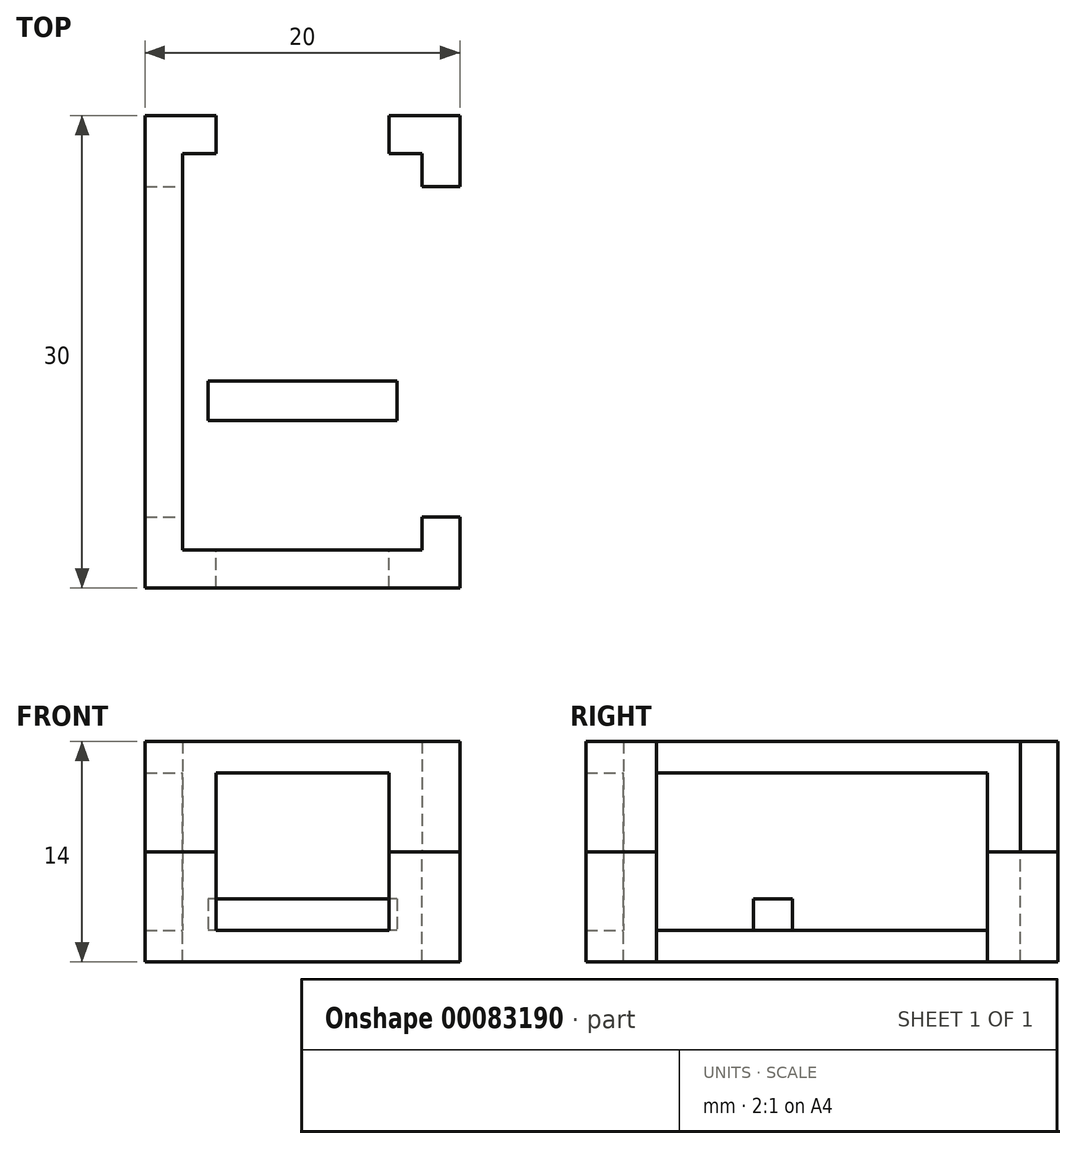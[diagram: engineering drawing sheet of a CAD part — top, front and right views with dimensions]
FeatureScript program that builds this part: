
annotation { "Feature Type Name" : "Feature", "Feature Type Description" : "" }
export const myFeature = defineFeature(function(context is Context, id is Id, definition is map)
    precondition{}
    {
        {
            var Q0;
            Q0=qCreatedBy(makeId("Top.planeOp"),FACE);
            var sketch = newSketch(context, id + "F0", { "sketchPlane" : qUnion([Q0])});
            skLineSegment(sketch, "E0.bottom", {"start": v(-38.64, -31.51) * mm, "end": v(-53.84, -31.51) * mm});
            skLineSegment(sketch, "E0.top", {"start": v(-38.64, -6.31) * mm, "end": v(-53.84, -6.31) * mm});
            skLineSegment(sketch, "E0.left", {"start": v(-38.64, -31.51) * mm, "end": v(-38.64, -6.31) * mm});
            skLineSegment(sketch, "E0.right", {"start": v(-53.84, -31.51) * mm, "end": v(-53.84, -6.31) * mm});
            skPoint(sketch, "E1", {"position": v(-49.44, -6.31) * mm});
            skPoint(sketch, "E2", {"position": v(-38.64, -27.41) * mm});
            skLineSegment(sketch, "E3.1.0.0", {"start": v(-38.64, -26.16) * mm, "end": v(-38.64, -25.16) * mm});
            skPoint(sketch, "E3.1.0.1", {"position": v(-38.64, -26.16) * mm});
            skLineSegment(sketch, "E3.2.0.0", {"start": v(-38.64, -24.91) * mm, "end": v(-38.64, -23.91) * mm});
            skPoint(sketch, "E3.2.0.1", {"position": v(-38.64, -24.91) * mm});
            skLineSegment(sketch, "E3.3.0.0", {"start": v(-38.64, -23.66) * mm, "end": v(-38.64, -22.66) * mm});
            skPoint(sketch, "E3.3.0.1", {"position": v(-38.64, -23.66) * mm});
            skLineSegment(sketch, "E4.0.8.0", {"start": v(-38.64, -17.41) * mm, "end": v(-38.64, -16.41) * mm});
            skPoint(sketch, "E4.3.8.0", {"position": v(-38.64, -17.41) * mm});
            skLineSegment(sketch, "E4.0.9.0", {"start": v(-38.64, -16.16) * mm, "end": v(-38.64, -15.16) * mm});
            skPoint(sketch, "E4.3.9.0", {"position": v(-38.64, -16.16) * mm});
            skLineSegment(sketch, "E5.bottom", {"start": v(-49.44, -6.31) * mm, "end": v(-48.44, -6.31) * mm});
            skPoint(sketch, "E6.1.0.1", {"position": v(-48.19, -6.31) * mm});
            skLineSegment(sketch, "E6.1.0.4", {"start": v(-48.19, -6.31) * mm, "end": v(-47.19, -6.31) * mm});
            skPoint(sketch, "E6.2.0.1", {"position": v(-46.94, -6.31) * mm});
            skLineSegment(sketch, "E6.2.0.4", {"start": v(-46.94, -6.31) * mm, "end": v(-45.94, -6.31) * mm});
            skPoint(sketch, "E6.3.0.1", {"position": v(-45.69, -6.31) * mm});
            skLineSegment(sketch, "E6.3.0.4", {"start": v(-45.69, -6.31) * mm, "end": v(-44.69, -6.31) * mm});
            skPoint(sketch, "E6.4.0.1", {"position": v(-44.44, -6.31) * mm});
            skLineSegment(sketch, "E6.4.0.4", {"start": v(-44.44, -6.31) * mm, "end": v(-43.44, -6.31) * mm});
            skLineSegment(sketch, "E7.bottom", {"start": v(-36.24, -33.91) * mm, "end": v(-56.24, -33.91) * mm});
            skLineSegment(sketch, "E7.top", {"start": v(-36.24, -3.91) * mm, "end": v(-56.24, -3.91) * mm});
            skLineSegment(sketch, "E7.left", {"start": v(-36.24, -33.91) * mm, "end": v(-36.24, -3.91) * mm});
            skLineSegment(sketch, "E7.right", {"start": v(-56.24, -33.91) * mm, "end": v(-56.24, -3.91) * mm});
            skLineSegment(sketch, "E8.bottom", {"start": v(-42.24, -16.16) * mm, "end": v(-50.24, -16.16) * mm});
            skLineSegment(sketch, "E8.top", {"start": v(-42.24, -8.66) * mm, "end": v(-50.24, -8.66) * mm});
            skLineSegment(sketch, "E8.left", {"start": v(-42.24, -16.16) * mm, "end": v(-42.24, -8.66) * mm});
            skLineSegment(sketch, "E8.right", {"start": v(-50.24, -16.16) * mm, "end": v(-50.24, -8.66) * mm});
            skPoint(sketch, "E9", {"position": v(-39.24, -24.41) * mm});
            skPoint(sketch, "E9.positionSnap0", {"position": v(-39.84, -24.41) * mm});
            skPoint(sketch, "E9.positionSnap1", {"position": v(-39.24, -24.91) * mm});
            skPoint(sketch, "E10", {"position": v(-39.24, -23.16) * mm});
            skPoint(sketch, "E10.positionSnap0", {"position": v(-39.84, -23.16) * mm});
            skPoint(sketch, "E10.positionSnap1", {"position": v(-39.24, -23.66) * mm});
            skPoint(sketch, "E11", {"position": v(-39.24, -16.91) * mm});
            skPoint(sketch, "E11.positionSnap0", {"position": v(-39.84, -16.91) * mm});
            skPoint(sketch, "E11.positionSnap1", {"position": v(-39.24, -17.41) * mm});
            skPoint(sketch, "E12", {"position": v(-39.24, -15.66) * mm});
            skPoint(sketch, "E12.positionSnap0", {"position": v(-39.84, -15.66) * mm});
            skPoint(sketch, "E12.positionSnap1", {"position": v(-39.24, -16.16) * mm});
            skPoint(sketch, "E13", {"position": v(-43.94, -6.91) * mm});
            skPoint(sketch, "E13.positionSnap0", {"position": v(-43.94, -7.51) * mm});
            skPoint(sketch, "E13.positionSnap1", {"position": v(-43.44, -6.91) * mm});
            skPoint(sketch, "E14", {"position": v(-45.19, -6.91) * mm});
            skPoint(sketch, "E14.positionSnap0", {"position": v(-45.19, -7.51) * mm});
            skPoint(sketch, "E14.positionSnap1", {"position": v(-45.69, -6.91) * mm});
            skPoint(sketch, "E15", {"position": v(-46.44, -6.91) * mm});
            skPoint(sketch, "E15.positionSnap0", {"position": v(-46.44, -7.51) * mm});
            skPoint(sketch, "E15.positionSnap1", {"position": v(-46.94, -6.91) * mm});
            skPoint(sketch, "E16", {"position": v(-47.69, -6.91) * mm});
            skPoint(sketch, "E16.positionSnap0", {"position": v(-47.69, -7.51) * mm});
            skPoint(sketch, "E16.positionSnap1", {"position": v(-47.19, -6.91) * mm});
            skPoint(sketch, "E17", {"position": v(-48.94, -6.91) * mm});
            skPoint(sketch, "E17.positionSnap0", {"position": v(-48.94, -6.31) * mm});
            skPoint(sketch, "E17.positionSnap1", {"position": v(-48.44, -6.91) * mm});
            skLineSegment(sketch, "E18", {"start": v(-56.24, -29.41) * mm, "end": v(-53.84, -29.41) * mm});
            skLineSegment(sketch, "E19", {"start": v(-51.74, -33.91) * mm, "end": v(-51.74, -31.51) * mm});
            skLineSegment(sketch, "E20.trimOffspring", {"start": v(-38.64, -29.41) * mm, "end": v(-36.24, -29.41) * mm});
            skLineSegment(sketch, "E21.trimOffspring", {"start": v(-51.74, -6.31) * mm, "end": v(-51.74, -3.91) * mm});
            skLineSegment(sketch, "E22.MirrorCS", {"start": v(-56.24, -8.41) * mm, "end": v(-53.84, -8.41) * mm});
            skLineSegment(sketch, "E23.MirrorCS", {"start": v(-38.64, -8.41) * mm, "end": v(-36.24, -8.41) * mm});
            skLineSegment(sketch, "E24.MirrorCS", {"start": v(-40.74, -33.91) * mm, "end": v(-40.74, -31.51) * mm});
            skLineSegment(sketch, "E25.MirrorCS", {"start": v(-40.74, -6.31) * mm, "end": v(-40.74, -3.91) * mm});
            skLineSegment(sketch, "E26", {"start": v(-53.84, -19.28) * mm, "end": v(-38.64, -19.28) * mm, "construction": true});
            skLineSegment(sketch, "E27", {"start": v(-53.84, -22.02) * mm, "end": v(-38.64, -22.02) * mm, "construction": true});
            skLineSegment(sketch, "E28", {"start": v(-53.84, -25.38) * mm, "end": v(-38.64, -25.38) * mm, "construction": true});
            skLineSegment(sketch, "E29", {"start": v(-53.84, -28.17) * mm, "end": v(-38.64, -28.17) * mm, "construction": true});
            skPoint(sketch, "E30", {"position": v(-49.84, -19.28) * mm});
            skPoint(sketch, "E31", {"position": v(-48.59, -19.28) * mm});
            skPoint(sketch, "E32", {"position": v(-43.89, -19.28) * mm});
            skPoint(sketch, "E33", {"position": v(-49.84, -22.02) * mm});
            skPoint(sketch, "E34", {"position": v(-48.59, -22.02) * mm});
            skPoint(sketch, "E35", {"position": v(-42.64, -22.02) * mm});
            skPoint(sketch, "E36", {"position": v(-43.89, -22.02) * mm});
            skPoint(sketch, "E37", {"position": v(-49.84, -25.38) * mm});
            skPoint(sketch, "E38", {"position": v(-48.59, -25.38) * mm});
            skPoint(sketch, "E39", {"position": v(-43.89, -25.38) * mm});
            skPoint(sketch, "E40", {"position": v(-42.64, -25.38) * mm});
            skPoint(sketch, "E41", {"position": v(-42.64, -19.28) * mm});
            skPoint(sketch, "E42", {"position": v(-39.24, -26.91) * mm});
            skPoint(sketch, "E43", {"position": v(-39.24, -25.66) * mm});
            skSolve(sketch);
        }
        {
            var Q0;
            Q0=makeQuery(id+"F0.imprint","IMPRINT",FACE,{"disambiguationData":[TD([[makeQuery(id+"F0.imprint","IMPRINT",EDGE,{"derivedFrom":sQuery(id+"F0.wireOp",EDGE,"5d814dad-614f-4d97-b61d-e02d43bfdc46")}),-1.0]])]});
            var Q1;
            {var subQ0=sQuery(id+"F0.wireOp",EDGE,"E18");Q1=makeQuery(id+"F0.imprint","IMPRINT",FACE,{"disambiguationData":[TD([[makeQuery(id+"F0.imprint","IMPRINT",EDGE,{"derivedFrom":subQ0}),1.0]])]});}
            var Q2;
            {var subQ0=sQuery(id+"F0.wireOp",EDGE,"E19");Q2=makeQuery(id+"F0.imprint","IMPRINT",FACE,{"disambiguationData":[TD([[makeQuery(id+"F0.imprint","IMPRINT",EDGE,{"derivedFrom":subQ0}),-1.0]])]});}
            var Q3;
            {var subQ3=sQuery(id+"F0.wireOp",EDGE,"E18");Q3=makeQuery(id+"F0.imprint","IMPRINT",FACE,{"disambiguationData":[TD([[makeQuery(id+"F0.imprint","IMPRINT",EDGE,{"derivedFrom":subQ3}),-1.0]])]});}
            var Q4;
            {var subQ4=sQuery(id+"F0.wireOp",EDGE,"E20.trimOffspring");Q4=makeQuery(id+"F0.imprint","IMPRINT",FACE,{"disambiguationData":[TD([[makeQuery(id+"F0.imprint","IMPRINT",EDGE,{"derivedFrom":subQ4}),-1.0]])]});}
            var Q5;
            {var subQ4=sQuery(id+"F0.wireOp",EDGE,"E3.1.0.0");Q5=makeQuery(id+"F0.imprint","IMPRINT",FACE,{"disambiguationData":[TD([[makeQuery(id+"F0.imprint","IMPRINT",EDGE,{"derivedFrom":subQ4}),-1.0]])]});}
            var Q6;
            {var subQ3=sQuery(id+"F0.wireOp",EDGE,"E23.MirrorCS");Q6=makeQuery(id+"F0.imprint","IMPRINT",FACE,{"disambiguationData":[TD([[makeQuery(id+"F0.imprint","IMPRINT",EDGE,{"derivedFrom":subQ3}),1.0]])]});}
            var Q7;
            {var subQ0=sQuery(id+"F0.wireOp",EDGE,"E5.bottom");Q7=makeQuery(id+"F0.imprint","IMPRINT",FACE,{"disambiguationData":[TD([[makeQuery(id+"F0.imprint","IMPRINT",EDGE,{"derivedFrom":subQ0}),1.0]])]});}
            var Q8;
            {var subQ7=sQuery(id+"F0.wireOp",EDGE,"E21.trimOffspring");Q8=makeQuery(id+"F0.imprint","IMPRINT",FACE,{"disambiguationData":[TD([[makeQuery(id+"F0.imprint","IMPRINT",EDGE,{"derivedFrom":subQ7}),1.0]])]});}
            var Q9;
            {var subQ4=sQuery(id+"F0.wireOp",EDGE,"E3.1.0.0");Q9=makeQuery(id+"F0.imprint","IMPRINT",FACE,{"disambiguationData":[TD([[makeQuery(id+"F0.imprint","IMPRINT",EDGE,{"derivedFrom":subQ4}),1.0]])]});}
            extrude(context, id + "F1", {"entities" : qUnion([Q0, Q1, Q2, Q3, Q4, Q5, Q6, Q7, Q8, Q9]), "oppositeDirection" : true, "depth" : 2 * mm});
        }
        {
            var Q0;
            {var subQ4=sQuery(id+"F0.wireOp",EDGE,"E21.trimOffspring");Q0=makeQuery(id+"F0.imprint","IMPRINT",FACE,{"disambiguationData":[TD([[makeQuery(id+"F0.imprint","IMPRINT",EDGE,{"derivedFrom":subQ4}),1.0]])]});}
            var Q1;
            {var subQ3=sQuery(id+"F0.wireOp",EDGE,"E23.MirrorCS");Q1=makeQuery(id+"F0.imprint","IMPRINT",FACE,{"disambiguationData":[TD([[makeQuery(id+"F0.imprint","IMPRINT",EDGE,{"derivedFrom":subQ3}),1.0]])]});}
            var Q2;
            {var subQ3=sQuery(id+"F0.wireOp",EDGE,"E20.trimOffspring");Q2=makeQuery(id+"F0.imprint","IMPRINT",FACE,{"disambiguationData":[TD([[makeQuery(id+"F0.imprint","IMPRINT",EDGE,{"derivedFrom":subQ3}),-1.0]])]});}
            var Q3;
            {var subQ3=sQuery(id+"F0.wireOp",EDGE,"E18");Q3=makeQuery(id+"F0.imprint","IMPRINT",FACE,{"disambiguationData":[TD([[makeQuery(id+"F0.imprint","IMPRINT",EDGE,{"derivedFrom":subQ3}),-1.0]])]});}
            extrude(context, id + "F2", {"entities" : qUnion([Q0, Q1, Q2, Q3]), "operationType" : NewBodyOperationType.ADD, "depth" : 5 * mm});
        }
        {
            var Q0;
            Q0=sQuery(id+"F0.wireOp",VERTEX,"E9");
            var Q1;
            Q1=sQuery(id+"F0.wireOp",VERTEX,"E10");
            var Q2;
            Q2=sQuery(id+"F0.wireOp",VERTEX,"E11");
            var Q3;
            Q3=sQuery(id+"F0.wireOp",VERTEX,"E12");
            var Q4;
            Q4=sQuery(id+"F0.wireOp",VERTEX,"E13");
            var Q5;
            Q5=sQuery(id+"F0.wireOp",VERTEX,"E14");
            var Q6;
            Q6=sQuery(id+"F0.wireOp",VERTEX,"E15");
            var Q7;
            Q7=sQuery(id+"F0.wireOp",VERTEX,"E16");
            var Q8;
            Q8=sQuery(id+"F0.wireOp",VERTEX,"E17");
            var Q9;
            Q9=sQuery(id+"F0.wireOp",VERTEX,"E43");
            var Q10;
            Q10=sQuery(id+"F0.wireOp",VERTEX,"E42");
            var Q11;
            Q11=makeQuery(id+"F1.opExtrude","SWEPT_BODY",BODY,{"disambiguationData":[OSD([sQuery(id+"F0.wireOp",EDGE,"E7.bottom"),sQuery(id+"F0.wireOp",EDGE,"E7.top"),sQuery(id+"F0.wireOp",EDGE,"E7.left"),sQuery(id+"F0.wireOp",EDGE,"E7.right"),sQuery(id+"F0.wireOp",EDGE,"E8.bottom"),sQuery(id+"F0.wireOp",EDGE,"E8.top"),sQuery(id+"F0.wireOp",EDGE,"E8.left"),sQuery(id+"F0.wireOp",EDGE,"E8.right")])]});
            hole(context, id + "F3", {"style" : HoleStyle.SIMPLE, "endStyle" : HoleEndStyle.THROUGH, "holeDiameter" : 1.1 * mm, "locations" : qUnion([Q0, Q1, Q2, Q3, Q4, Q5, Q6, Q7, Q8, Q9, Q10]), "scope" : qUnion([Q11]), "isTappedThrough" : true});
        }
        {
            var Q0;
            Q0=sQuery(id+"F0.wireOp",VERTEX,"E30");
            var Q1;
            Q1=sQuery(id+"F0.wireOp",VERTEX,"E31");
            var Q2;
            Q2=sQuery(id+"F0.wireOp",VERTEX,"E32");
            var Q3;
            Q3=sQuery(id+"F0.wireOp",VERTEX,"E41");
            var Q4;
            Q4=sQuery(id+"F0.wireOp",VERTEX,"E33");
            var Q5;
            Q5=sQuery(id+"F0.wireOp",VERTEX,"E34");
            var Q6;
            Q6=sQuery(id+"F0.wireOp",VERTEX,"E36");
            var Q7;
            Q7=sQuery(id+"F0.wireOp",VERTEX,"E35");
            var Q8;
            Q8=makeQuery(id+"F1.opExtrude","SWEPT_BODY",BODY,{"disambiguationData":[OSD([sQuery(id+"F0.wireOp",EDGE,"E7.bottom"),sQuery(id+"F0.wireOp",EDGE,"E7.top"),sQuery(id+"F0.wireOp",EDGE,"E7.left"),sQuery(id+"F0.wireOp",EDGE,"E7.right"),sQuery(id+"F0.wireOp",EDGE,"E8.bottom"),sQuery(id+"F0.wireOp",EDGE,"E8.top"),sQuery(id+"F0.wireOp",EDGE,"E8.left"),sQuery(id+"F0.wireOp",EDGE,"E8.right")])]});
            hole(context, id + "F4", {"style" : HoleStyle.SIMPLE, "endStyle" : HoleEndStyle.THROUGH, "holeDiameter" : 1.1 * mm, "locations" : qUnion([Q0, Q1, Q2, Q3, Q4, Q5, Q6, Q7]), "scope" : qUnion([Q8]), "isTappedThrough" : true});
        }
        {
            var Q0;
            Q0=sQuery(id+"F0.wireOp",VERTEX,"E37");
            var Q1;
            Q1=sQuery(id+"F0.wireOp",VERTEX,"E38");
            var Q2;
            Q2=sQuery(id+"F0.wireOp",VERTEX,"E39");
            var Q3;
            Q3=sQuery(id+"F0.wireOp",VERTEX,"E40");
            var Q4;
            Q4=makeQuery(id+"F1.opExtrude","SWEPT_BODY",BODY,{"disambiguationData":[OSD([sQuery(id+"F0.wireOp",EDGE,"E7.bottom"),sQuery(id+"F0.wireOp",EDGE,"E7.top"),sQuery(id+"F0.wireOp",EDGE,"E7.left"),sQuery(id+"F0.wireOp",EDGE,"E7.right"),sQuery(id+"F0.wireOp",EDGE,"E8.bottom"),sQuery(id+"F0.wireOp",EDGE,"E8.top"),sQuery(id+"F0.wireOp",EDGE,"E8.left"),sQuery(id+"F0.wireOp",EDGE,"E8.right")])]});
            hole(context, id + "F5", {"style" : HoleStyle.SIMPLE, "endStyle" : HoleEndStyle.THROUGH, "holeDiameter" : 1 * mm, "locations" : qUnion([Q0, Q1, Q2, Q3]), "scope" : qUnion([Q4]), "isTappedThrough" : true});
        }
        {
            var Q0;
            Q0=makeQuery(id+"F1.opExtrude","CAP_FACE",FACE,{"disambiguationData":[OSD([sQuery(id+"F0.wireOp",EDGE,"E7.bottom"),sQuery(id+"F0.wireOp",EDGE,"E7.top"),sQuery(id+"F0.wireOp",EDGE,"E7.left"),sQuery(id+"F0.wireOp",EDGE,"E7.right"),sQuery(id+"F0.wireOp",EDGE,"E8.bottom"),sQuery(id+"F0.wireOp",EDGE,"E8.top"),sQuery(id+"F0.wireOp",EDGE,"E8.left"),sQuery(id+"F0.wireOp",EDGE,"E8.right")])],"isStart":true});
            var sketch = newSketch(context, id + "F6", { "sketchPlane" : qUnion([Q0])});
            skLineSegment(sketch, "E44.bottom", {"start": v(-41.24, -22.67) * mm, "end": v(-51.24, -22.67) * mm});
            skLineSegment(sketch, "E44.top", {"start": v(-41.24, -21.37) * mm, "end": v(-51.24, -21.37) * mm});
            skLineSegment(sketch, "E44.left", {"start": v(-41.24, -22.67) * mm, "end": v(-41.24, -21.37) * mm});
            skLineSegment(sketch, "E44.right", {"start": v(-51.24, -22.67) * mm, "end": v(-51.24, -21.37) * mm});
            skPoint(sketch, "E44.middle", {"position": v(-46.24, -22.02) * mm});
            skPoint(sketch, "E44.middle.positionSnap0", {"position": v(-46.24, -16.16) * mm});
            skPoint(sketch, "E44.centerSnap0", {"position": v(-46.24, -16.16) * mm});
            skPoint(sketch, "E45", {"position": v(-43.89, -22.02) * mm});
            skLineSegment(sketch, "E46.bottom", {"start": v(-40.24, -23.27) * mm, "end": v(-52.24, -23.27) * mm});
            skLineSegment(sketch, "E46.top", {"start": v(-40.24, -20.77) * mm, "end": v(-52.24, -20.77) * mm});
            skLineSegment(sketch, "E46.left", {"start": v(-40.24, -23.27) * mm, "end": v(-40.24, -20.77) * mm});
            skLineSegment(sketch, "E46.right", {"start": v(-52.24, -23.27) * mm, "end": v(-52.24, -20.77) * mm});
            skLineSegment(sketch, "E47", {"start": v(-41.24, -21.42) * mm, "end": v(-46.24, -21.42) * mm});
            skLineSegment(sketch, "E48", {"start": v(-46.24, -21.37) * mm, "end": v(-46.24, -21.42) * mm});
            skLineSegment(sketch, "E49", {"start": v(-46.24, -22.62) * mm, "end": v(-41.24, -22.62) * mm});
            skLineSegment(sketch, "E50.trimOffspring", {"start": v(-46.24, -22.62) * mm, "end": v(-46.24, -22.67) * mm});
            skSolve(sketch);
        }
        {
            var Q0;
            Q0=makeQuery(id+"F1.opExtrude","CAP_FACE",FACE,{"disambiguationData":[OSD([sQuery(id+"F0.wireOp",EDGE,"E7.bottom"),sQuery(id+"F0.wireOp",EDGE,"E7.top"),sQuery(id+"F0.wireOp",EDGE,"E7.left"),sQuery(id+"F0.wireOp",EDGE,"E7.right"),sQuery(id+"F0.wireOp",EDGE,"E8.bottom"),sQuery(id+"F0.wireOp",EDGE,"E8.top"),sQuery(id+"F0.wireOp",EDGE,"E8.left"),sQuery(id+"F0.wireOp",EDGE,"E8.right")])],"isStart":false});
            var sketch = newSketch(context, id + "F7", { "sketchPlane" : qUnion([Q0])});
            skLineSegment(sketch, "E51.bottom", {"start": v(-41.24, 21.37) * mm, "end": v(-51.24, 21.37) * mm});
            skLineSegment(sketch, "E51.top", {"start": v(-41.24, 22.67) * mm, "end": v(-51.24, 22.67) * mm});
            skLineSegment(sketch, "E51.left", {"start": v(-41.24, 21.37) * mm, "end": v(-41.24, 22.67) * mm});
            skLineSegment(sketch, "E51.right", {"start": v(-51.24, 21.37) * mm, "end": v(-51.24, 22.67) * mm});
            skPoint(sketch, "E51.middle", {"position": v(-46.24, 22.02) * mm});
            skPoint(sketch, "E51.middle.positionSnap0", {"position": v(-46.24, 27.88) * mm});
            skPoint(sketch, "E51.centerSnap0", {"position": v(-46.24, 27.88) * mm});
            skPoint(sketch, "E52", {"position": v(-43.89, 22.02) * mm});
            skLineSegment(sketch, "E53.bottom", {"start": v(-40.24, 20.77) * mm, "end": v(-52.24, 20.77) * mm});
            skLineSegment(sketch, "E53.top", {"start": v(-40.24, 23.27) * mm, "end": v(-52.24, 23.27) * mm});
            skLineSegment(sketch, "E53.left", {"start": v(-40.24, 20.77) * mm, "end": v(-40.24, 23.27) * mm});
            skLineSegment(sketch, "E53.right", {"start": v(-52.24, 20.77) * mm, "end": v(-52.24, 23.27) * mm});
            skLineSegment(sketch, "E54", {"start": v(-41.24, 22.62) * mm, "end": v(-46.24, 22.62) * mm});
            skLineSegment(sketch, "E55", {"start": v(-46.24, 22.67) * mm, "end": v(-46.24, 22.62) * mm});
            skLineSegment(sketch, "E56", {"start": v(-46.24, 21.42) * mm, "end": v(-41.24, 21.42) * mm});
            skLineSegment(sketch, "E57.trimOffspring", {"start": v(-46.24, 21.42) * mm, "end": v(-46.24, 21.37) * mm});
            skSolve(sketch);
        }
        {
            var Q0;
            {var subQ0=sQuery(id+"F6.wireOp",EDGE,"E44.right");Q0=makeQuery(id+"F6.imprint","IMPRINT",FACE,{"disambiguationData":[TD([[makeQuery(id+"F6.imprint","IMPRINT",EDGE,{"derivedFrom":subQ0}),1.0]])]});}
            var Q1;
            {var subQ4=sQuery(id+"F6.wireOp",EDGE,"E44.right");Q1=makeQuery(id+"F6.imprint","IMPRINT",FACE,{"disambiguationData":[TD([[makeQuery(id+"F6.imprint","IMPRINT",EDGE,{"derivedFrom":subQ4}),-1.0]])]});}
            var Q2;
            {var subQ4=sQuery(id+"F6.wireOp",EDGE,"E47");Q2=makeQuery(id+"F6.imprint","IMPRINT",FACE,{"disambiguationData":[TD([[makeQuery(id+"F6.imprint","IMPRINT",EDGE,{"derivedFrom":subQ4}),-1.0]])]});}
            var Q3;
            {var subQ4=sQuery(id+"F6.wireOp",EDGE,"E49");Q3=makeQuery(id+"F6.imprint","IMPRINT",FACE,{"disambiguationData":[TD([[makeQuery(id+"F6.imprint","IMPRINT",EDGE,{"derivedFrom":subQ4}),-1.0]])]});}
            extrude(context, id + "F8", {"entities" : qUnion([Q0, Q1, Q2, Q3]), "operationType" : NewBodyOperationType.ADD, "depth" : 2 * mm});
        }
        {
            var Q0;
            {var subQ1=sQuery(id+"F7.wireOp",EDGE,"E51.right");Q0=makeQuery(id+"F7.imprint","IMPRINT",FACE,{"disambiguationData":[TD([[makeQuery(id+"F7.imprint","IMPRINT",EDGE,{"derivedFrom":subQ1}),-1.0]])]});}
            extrude(context, id + "F9", {"entities" : qUnion([Q0]), "operationType" : NewBodyOperationType.REMOVE, "oppositeDirection" : true, "depth" : 2 * mm});
        }
        {
            var Q0;
            Q0=makeQuery(id+"F1.opExtrude","SWEPT_BODY",BODY,{"disambiguationData":[OSD([sQuery(id+"F0.wireOp",EDGE,"E7.bottom"),sQuery(id+"F0.wireOp",EDGE,"E7.top"),sQuery(id+"F0.wireOp",EDGE,"E7.left"),sQuery(id+"F0.wireOp",EDGE,"E7.right"),sQuery(id+"F0.wireOp",EDGE,"E8.bottom"),sQuery(id+"F0.wireOp",EDGE,"E8.top"),sQuery(id+"F0.wireOp",EDGE,"E8.left"),sQuery(id+"F0.wireOp",EDGE,"E8.right")])]});
            var Q1;
            Q1=makeQuery(id+"F2.opExtrude","CAP_FACE",FACE,{"disambiguationData":[OSD([sQuery(id+"F0.wireOp",EDGE,"E0.top"),sQuery(id+"F0.wireOp",EDGE,"E0.right"),sQuery(id+"F0.wireOp",EDGE,"E7.top"),sQuery(id+"F0.wireOp",EDGE,"E7.right"),sQuery(id+"F0.wireOp",EDGE,"E21.trimOffspring"),sQuery(id+"F0.wireOp",EDGE,"E22.MirrorCS")])],"isStart":false});
            mirror(context, id + "F10", {"entities" : qUnion([Q0]), "mirrorPlane" : qUnion([Q1])});
        }
    });
